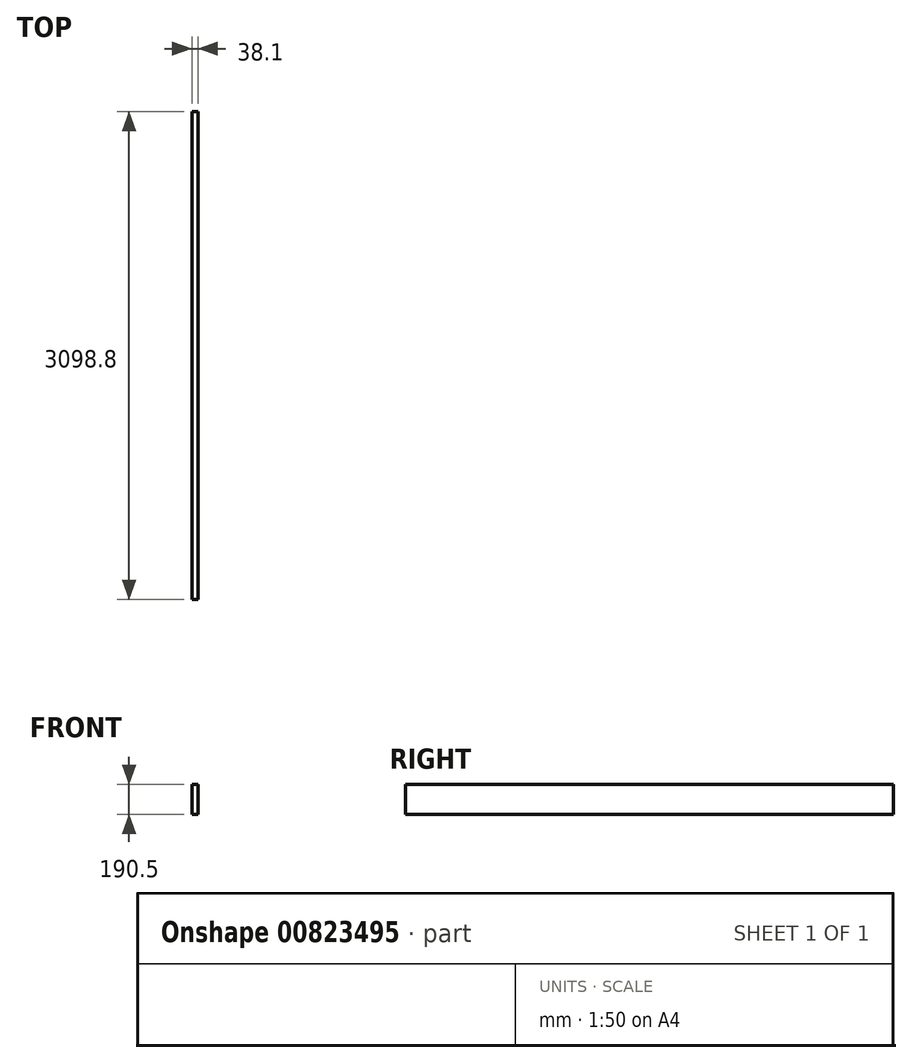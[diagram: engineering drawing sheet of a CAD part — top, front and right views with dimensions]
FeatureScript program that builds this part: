
annotation { "Feature Type Name" : "Feature", "Feature Type Description" : "" }
export const myFeature = defineFeature(function(context is Context, id is Id, definition is map)
    precondition{}
    {
        {
            var Q0;
            Q0=qCreatedBy(makeId("Front.planeOp"),FACE);
            var sketch = newSketch(context, id + "F0", { "sketchPlane" : qUnion([Q0])});
            skLineSegment(sketch, "E0.bottom", {"start": v(0, 0) * mm, "end": v(38.1, 0) * mm});
            skLineSegment(sketch, "E0.top", {"start": v(0, 190.5) * mm, "end": v(38.1, 190.5) * mm});
            skLineSegment(sketch, "E0.left", {"start": v(0, 0) * mm, "end": v(0, 190.5) * mm});
            skLineSegment(sketch, "E0.right", {"start": v(38.1, 0) * mm, "end": v(38.1, 190.5) * mm});
            skSolve(sketch);
        }
        {
            var Q0;
            Q0=qSketchRegion(id+"F0",true);
            extrude(context, id + "F1", {"entities" : qUnion([Q0]), "depth" : 3098.8 * mm, "offsetDistance" : 25.4 * mm});
        }
    });
